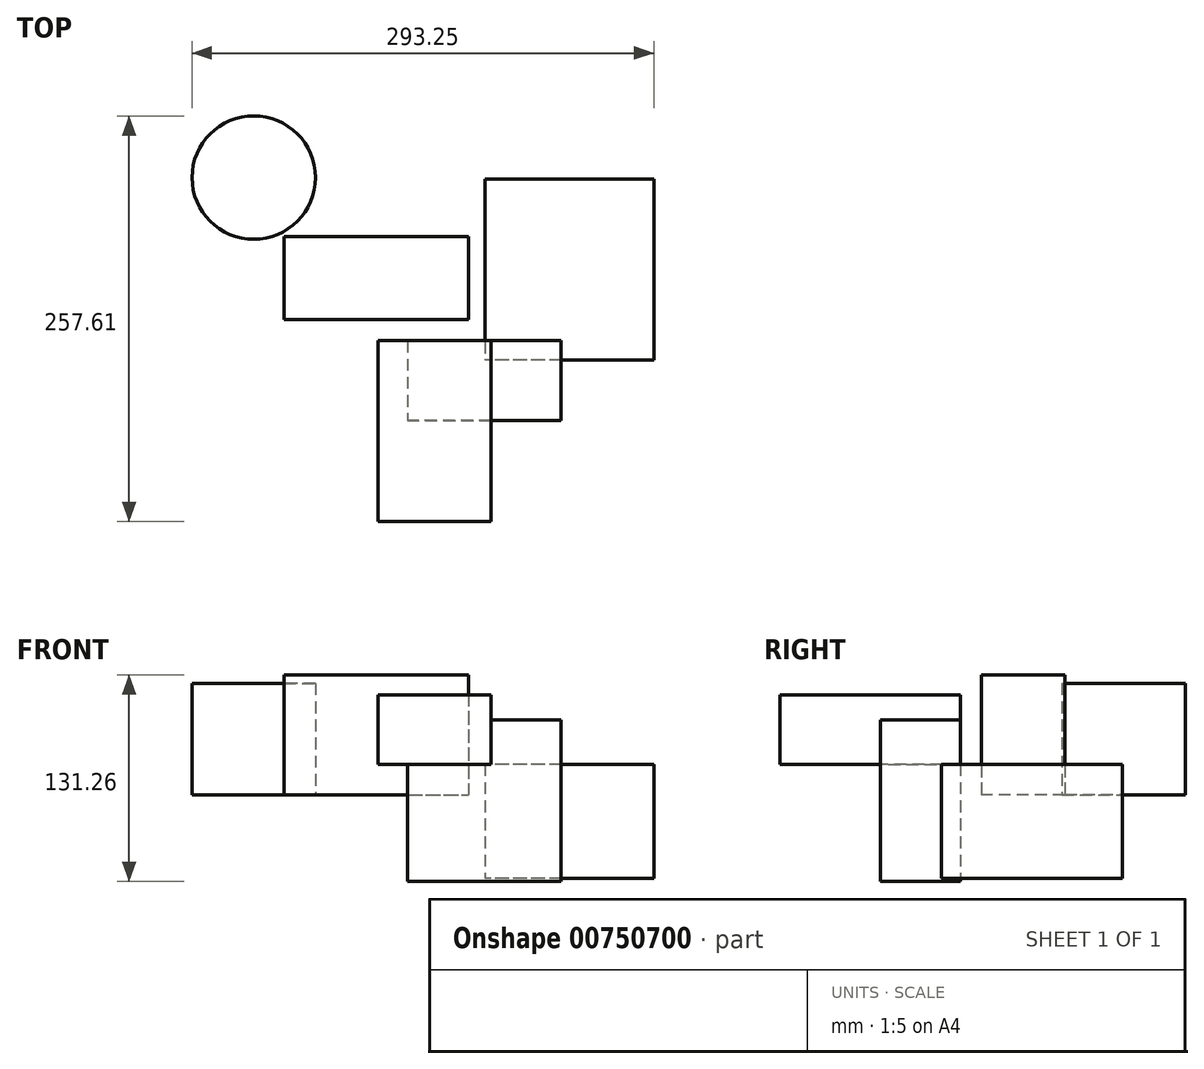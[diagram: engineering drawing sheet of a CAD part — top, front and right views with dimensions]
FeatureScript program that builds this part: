
annotation { "Feature Type Name" : "Feature", "Feature Type Description" : "" }
export const myFeature = defineFeature(function(context is Context, id is Id, definition is map)
    precondition{}
    {
        {
            var Q0;
            Q0=qCreatedBy(makeId("Front.planeOp"),FACE);
            var sketch = newSketch(context, id + "F0", { "sketchPlane" : qUnion([Q0])});
            skLineSegment(sketch, "E0.bottom", {"start": v(-230.78, -18.97) * mm, "end": v(-199.58, -18.97) * mm});
            skLineSegment(sketch, "E0.top", {"start": v(-230.78, -13.7) * mm, "end": v(-199.58, -13.7) * mm});
            skLineSegment(sketch, "E0.left", {"start": v(-230.78, -18.97) * mm, "end": v(-230.78, -13.7) * mm});
            skLineSegment(sketch, "E0.right", {"start": v(-199.58, -18.97) * mm, "end": v(-199.58, -13.7) * mm});
            skLineSegment(sketch, "E1.bottom", {"start": v(-49.34, 47.65) * mm, "end": v(48.33, 47.65) * mm});
            skLineSegment(sketch, "E1.top", {"start": v(-49.34, -55.06) * mm, "end": v(48.33, -55.06) * mm});
            skLineSegment(sketch, "E1.left", {"start": v(-49.34, 47.65) * mm, "end": v(-49.34, -55.06) * mm});
            skLineSegment(sketch, "E1.right", {"start": v(48.33, 47.65) * mm, "end": v(48.33, -55.06) * mm});
            skSolve(sketch);
        }
        {
            var Q0;
            Q0=makeQuery(id+"F0.imprint","IMPRINT",FACE,{"disambiguationData":[TD([[makeQuery(id+"F0.imprint","IMPRINT",EDGE,{"derivedFrom":sQuery(id+"F0.wireOp",EDGE,"E1.bottom")}),-1.0]])]});
            extrude(context, id + "F1", {"entities" : qUnion([Q0]), "depth" : 50.8 * mm, "offsetDistance" : 25.4 * mm});
        }
        {
            var Q0;
            Q0=qCreatedBy(makeId("Front.planeOp"),FACE);
            var sketch = newSketch(context, id + "F2", { "sketchPlane" : qUnion([Q0])});
            skLineSegment(sketch, "E2.bottom", {"start": v(-68.09, 63.6) * mm, "end": v(3.72, 63.6) * mm});
            skLineSegment(sketch, "E2.top", {"start": v(-68.09, 19.5) * mm, "end": v(3.72, 19.5) * mm});
            skLineSegment(sketch, "E2.left", {"start": v(-68.09, 63.6) * mm, "end": v(-68.09, 19.5) * mm});
            skLineSegment(sketch, "E2.right", {"start": v(3.72, 63.6) * mm, "end": v(3.72, 19.5) * mm});
            skSolve(sketch);
        }
        {
            var Q0;
            Q0=qCreatedBy(makeId("Top.planeOp"),FACE);
            var sketch = newSketch(context, id + "F3", { "sketchPlane" : qUnion([Q0])});
            skLineSegment(sketch, "E3.bottom", {"start": v(-127.72, 66.28) * mm, "end": v(-10.51, 66.28) * mm});
            skLineSegment(sketch, "E3.top", {"start": v(-127.72, 13.33) * mm, "end": v(-10.51, 13.33) * mm});
            skLineSegment(sketch, "E3.left", {"start": v(-127.72, 66.28) * mm, "end": v(-127.72, 13.33) * mm});
            skLineSegment(sketch, "E3.right", {"start": v(-10.51, 66.28) * mm, "end": v(-10.51, 13.33) * mm});
            skSolve(sketch);
        }
        {
            var Q0;
            Q0=makeQuery(id+"F2.imprint","IMPRINT",FACE,{"disambiguationData":[TD([[makeQuery(id+"F2.imprint","IMPRINT",EDGE,{"derivedFrom":sQuery(id+"F2.wireOp",EDGE,"E2.bottom")}),-1.0]])]});
            extrude(context, id + "F4", {"entities" : qUnion([Q0]), "operationType" : NewBodyOperationType.ADD, "depth" : 114.8 * mm, "offsetDistance" : 25.4 * mm});
        }
        {
            var Q0;
            Q0=makeQuery(id+"F3.imprint","IMPRINT",FACE,{"disambiguationData":[TD([[makeQuery(id+"F3.imprint","IMPRINT",EDGE,{"derivedFrom":sQuery(id+"F3.wireOp",EDGE,"E3.bottom")}),-1.0]])]});
            extrude(context, id + "F5", {"entities" : qUnion([Q0]), "depth" : 76.2 * mm, "offsetDistance" : 25.4 * mm});
        }
        {
            var Q0;
            Q0=qCreatedBy(makeId("Right.planeOp"),FACE);
            var sketch = newSketch(context, id + "F6", { "sketchPlane" : qUnion([Q0])});
            skLineSegment(sketch, "E4.bottom", {"start": v(102.72, 19.54) * mm, "end": v(-12.1, 19.54) * mm});
            skLineSegment(sketch, "E4.top", {"start": v(102.72, -52.94) * mm, "end": v(-12.1, -52.94) * mm});
            skLineSegment(sketch, "E4.left", {"start": v(102.72, 19.54) * mm, "end": v(102.72, -52.94) * mm});
            skLineSegment(sketch, "E4.right", {"start": v(-12.1, 19.54) * mm, "end": v(-12.1, -52.94) * mm});
            skSolve(sketch);
        }
        {
            var Q0;
            Q0=makeQuery(id+"F6.imprint","IMPRINT",FACE,{"disambiguationData":[TD([[makeQuery(id+"F6.imprint","IMPRINT",EDGE,{"derivedFrom":sQuery(id+"F6.wireOp",EDGE,"E4.bottom")}),1.0]])]});
            extrude(context, id + "F7", {"entities" : qUnion([Q0]), "depth" : 107.19 * mm, "offsetDistance" : 25.4 * mm});
        }
        {
            var Q0;
            Q0=qCreatedBy(makeId("Top.planeOp"),FACE);
            var sketch = newSketch(context, id + "F8", { "sketchPlane" : qUnion([Q0])});
            skCircle(sketch, "E5", {"center": v(-146.88, 103.61) * mm, "radius": 39.18 * mm});
            skSolve(sketch);
        }
        {
            var Q0;
            Q0 = qSketchRegion(id + "F8", true);
            extrude(context, id + "F9", {"entities" : qUnion([Q0]), "depth" : 70.87 * mm, "offsetDistance" : 25.4 * mm});
        }
    });
